# Revit family: Sensor-Lutron-Ceiling-LOS_C_Series-Occupancy-LOS-CDT-2000-WH
name_source: partatom
category: Lighting Devices
units: mm (PartAtom-declared; Revit-internal decimal feet)

## family parameters
Cut with Voids When Loaded = No
Host = Face
Maintain Annotation Orientation = Yes
OmniClass Number = 23.85.80.11.27
OmniClass Title = Lighting Controls
Part Type = Normal
Room Calculation Point = No
Round Connector Dimension = Use Diameter
Shared = No

## types (1)
- LOS-CDT-2000-WH
    Assembly Code = D5030800
    Cost = 0 $
    Coverage = 2000.00 SF
    Coverage Area = 2000 sqft (186 m2)
    Default Elevation = 0' - 0"
    Depth = 0' - 1 51/128"
    Description = Dual Technology Ceiling Mount Sensor
    Field of View = 360.00°
    Finish = Plastic - Lutron - White Gloss
    Instruction Sheet Link = https://assets.lutron.com
    Keynote = 16500
    Length = 0' - 4 1/2"
    Major Motion Coverage Range = PIR: 44 ft Diameter at 9 ft mounting Height  / Ultrasonic: 64 ft x 32 ft
    Manufacturer = Lutron Electronics Co., Inc
    Manufacturer Fax Number = 610-282-1243
    Maximum Operating Temperature = 104 °F
    Minimum Operating Temperature = 32 °F
    Minor Motion Coverage Range = PIR: 24 ft Diameter at 9 ft mounting Height  / Ultrasonic: 45 ft x 23 ft
    Model = LOS-CDT-2000-WH
    Performance URL = https://www.lutron.com
    Product Documentation Link = https://assets.lutron.com
    Product Name = LOS-C Series Dual Technology Ceiling Mount Sensor
    Product Page URL = https://www.lutron.com
    Sensor Material = Plastic - Lutron - White Gloss
    Sensor Type = Occupancy
    Series = LOS C Series
    Type Comments = -
    URL = http://www.lutron.com
    Version = 2021 - v1.0a
    Video Link = https://www.youtube.com
    Voltage = 20 V
    Voltage Comments = Operating voltage: 20 – 24 V-, IEC PELV/NECR Class 2
    Warranty URL = https://www.lutron.com
    Width = 0' - 4 1/2"

## geometry (parser evidence)
native form markers: Sweep x7
no freeform markers — native parametric forms only
